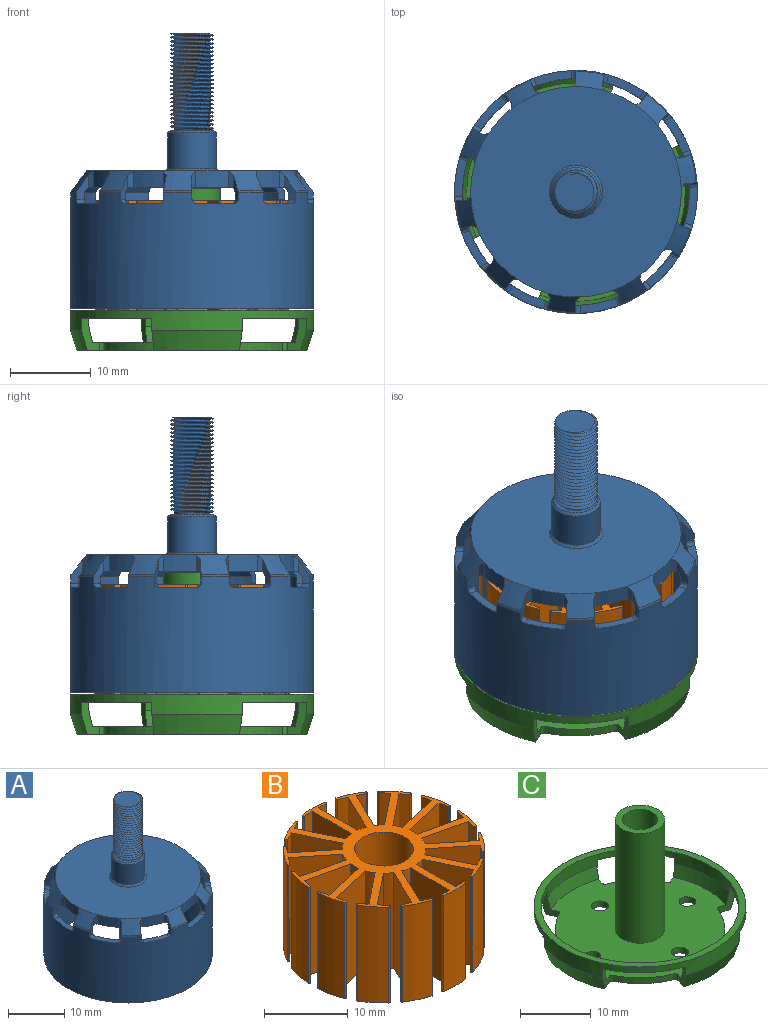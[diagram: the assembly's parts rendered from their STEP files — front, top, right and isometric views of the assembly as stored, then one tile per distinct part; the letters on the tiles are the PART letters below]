
ASSEMBLY  parts=3 mates=2
PART A: 126 faces, bbox 30.5x30.6x39.7 mm
  f0: bspline ~12.08x6.06mm, area 172.5mm2, adj f1,f2,f59,f60
  f1: bspline ~12.25x6.06mm, area 176.6mm2, adj f0,f2,f59,f60
  f2: cylinder r=2.2mm len=12mm, axis (0,0,-1), area -13.2mm2, adj f0,f1,f58,f59,f60
  f3: cylinder r=13mm len=4.02mm, axis (0,0,1), area 8.2mm2, adj f23,f56,f74,f75
  f4: cylinder r=13mm len=3mm, axis (0,0,1), area 8.2mm2, adj f23,f56,f71,f76
  f5: cylinder r=13mm len=4.07mm, axis (0,0,1), area 8.2mm2, adj f23,f56,f77,f78
  f6: cylinder r=13mm len=3.57mm, axis (0,0,1), area 8.2mm2, adj f23,f56,f79,f80
  f7: cylinder r=13mm len=3.72mm, axis (0,0,1), area 8.2mm2, adj f23,f56,f81,f82
  f8: cylinder r=13mm len=4.02mm, axis (0,0,1), area 8.2mm2, adj f23,f56,f83,f84
  f9: cylinder r=13mm len=3mm, axis (0,0,1), area 8.2mm2, adj f23,f56,f85,f86
  f10: cylinder r=13mm len=4.07mm, axis (0,0,1), area 8.2mm2, adj f23,f56,f87,f88
  f11: cylinder r=13mm len=3.57mm, axis (0,0,1), area 8.2mm2, adj f23,f56,f89,f90
  f12: cylinder r=13mm len=3.72mm, axis (0,0,1), area 8.2mm2, adj f23,f56,f72,f73
  f13: cone r=13mm half-angle=38.7deg, axis (0,0,-1), area 10.4mm2, adj f23,f26,f54,f73,f75,f120
  f14: cone r=13mm half-angle=38.7deg, axis (0,0,-1), area 10.4mm2, adj f23,f51,f53,f72,f89,f91
  f15: cone r=13mm half-angle=38.7deg, axis (0,0,-1), area 10.4mm2, adj f23,f48,f50,f88,f90,f94
  f16: cone r=13mm half-angle=38.7deg, axis (0,0,-1), area 10.4mm2, adj f23,f45,f47,f85,f87,f97
  f17: cone r=13mm half-angle=38.7deg, axis (0,0,-1), area 10.4mm2, adj f23,f42,f44,f83,f86,f100
  f18: cone r=13mm half-angle=38.7deg, axis (0,0,-1), area 10.4mm2, adj f23,f39,f41,f82,f84,f103
  f19: cone r=13mm half-angle=38.7deg, axis (0,0,-1), area 10.4mm2, adj f23,f36,f38,f79,f81,f106
  f20: cone r=13mm half-angle=38.7deg, axis (0,0,-1), area 10.4mm2, adj f23,f33,f35,f77,f80,f109
  f21: cone r=13mm half-angle=38.7deg, axis (0,0,-1), area 10.4mm2, adj f23,f30,f32,f71,f78,f112
  f22: cylinder r=15mm len=30mm, axis (0,0,-1), area 1275mm2, adj f25,f26,f27,f28,f29,f30,f31,f32
  f23: plane 26x26mm, normal (0,0,1), area 496.7mm2, adj f3,f4,f5,f6,f7,f8,f9,f10
  f24: cone r=13mm half-angle=38.7deg, axis (0,0,-1), area 10.4mm2, adj f23,f27,f29,f74,f76,f115
  f25: plane 4.74x1.86mm, normal (0,0,1), area 4.7mm2, adj f22,f55,f118,f119
  f26: plane 2.89x1.51mm, normal (1,0,0), area 2.3mm2, adj f13,f22,f55,f56,f70,f75,f119,f120
  f27: plane 2.89x1.4mm, normal (-0.92,-0.38,0), area 2.3mm2, adj f22,f24,f55,f56,f68,f74,f115,f118
  f28: plane 4.07x3.87mm, normal (0,0,1), area 4.7mm2, adj f22,f55,f116,f117
  f29: plane 2.89x1.22mm, normal (0.81,0.59,0), area 2.3mm2, adj f22,f24,f55,f56,f68,f76,f115,f117
  f30: plane 2.89x1.29mm, normal (-0.52,-0.85,0), area 2.3mm2, adj f21,f22,f55,f56,f67,f71,f112,f116
  f31: plane 4.8x1.54mm, normal (0,0,1), area 4.7mm2, adj f22,f55,f113,f114
  f32: plane 2.89x1.44mm, normal (0.31,0.95,0), area 2.3mm2, adj f21,f22,f55,f56,f67,f78,f112,f114
  f33: plane 2.89x1.51mm, normal (0.08,-1,0), area 2.3mm2, adj f20,f22,f55,f56,f61,f77,f109,f113
  f34: plane 4.53x3.12mm, normal (0,0,1), area 4.7mm2, adj f22,f55,f110,f111
  f35: plane 2.89x1.44mm, normal (-0.31,0.95,0), area 2.3mm2, adj f20,f22,f55,f56,f61,f80,f109,f111
  f36: plane 2.89x1.15mm, normal (0.65,-0.76,0), area 2.3mm2, adj f19,f22,f55,f56,f62,f79,f106,f110
  f37: plane 4.62x2.84mm, normal (0,0,1), area 4.7mm2, adj f22,f55,f107,f108
  f38: plane 2.89x1.22mm, normal (-0.81,0.59,0), area 2.3mm2, adj f19,f22,f55,f56,f62,f81,f106,f108
  f39: plane 2.89x1.47mm, normal (0.97,-0.24,0), area 2.3mm2, adj f18,f22,f55,f56,f63,f82,f103,f107
  f40: plane 4.74x1.86mm, normal (0,0,1), area 4.7mm2, adj f22,f55,f104,f105
  f41: plane 2.89x1.51mm, normal (-1,0,0), area 2.3mm2, adj f18,f22,f55,f56,f63,f84,f103,f105
  f42: plane 2.89x1.4mm, normal (0.92,0.38,0), area 2.3mm2, adj f17,f22,f55,f56,f64,f83,f100,f104
  f43: plane 4.07x3.87mm, normal (0,0,1), area 4.7mm2, adj f22,f55,f101,f102
  f44: plane 2.89x1.22mm, normal (-0.81,-0.59,0), area 2.3mm2, adj f17,f22,f55,f56,f64,f86,f100,f102
  f45: plane 2.89x1.29mm, normal (0.52,0.85,0), area 2.3mm2, adj f16,f22,f55,f56,f65,f85,f97,f101
  f46: plane 4.8x1.54mm, normal (0,0,1), area 4.7mm2, adj f22,f55,f98,f99
  f47: plane 2.89x1.44mm, normal (-0.31,-0.95,0), area 2.3mm2, adj f16,f22,f55,f56,f65,f87,f97,f99
  f48: plane 2.89x1.51mm, normal (-0.08,1,0), area 2.3mm2, adj f15,f22,f55,f56,f66,f88,f94,f98
  f49: plane 4.53x3.12mm, normal (0,0,1), area 4.7mm2, adj f22,f55,f95,f96
  f50: plane 2.89x1.44mm, normal (0.31,-0.95,0), area 2.3mm2, adj f15,f22,f55,f56,f66,f90,f94,f96
  f51: plane 2.89x1.15mm, normal (-0.65,0.76,0), area 2.3mm2, adj f14,f22,f55,f56,f69,f89,f91,f95
  f52: plane 4.62x2.84mm, normal (0,0,1), area 4.7mm2, adj f22,f55,f92,f93
  f53: plane 2.89x1.22mm, normal (0.81,-0.59,0), area 2.3mm2, adj f14,f22,f55,f56,f69,f72,f91,f93
  f54: plane 2.89x1.47mm, normal (-0.97,0.24,0), area 2.3mm2, adj f13,f22,f55,f56,f70,f73,f92,f120
  f55: cylinder r=14mm len=28mm, axis (0,0,-1), area 1189.4mm2, adj f25,f26,f27,f28,f29,f30,f31,f32
  f56: plane 27x26.92mm, normal (0,0,-1), area 542mm2, adj f3,f4,f5,f6,f7,f8,f9,f10
  f57: cylinder r=3mm len=6mm, axis (0,0,-1), area 82.9mm2, adj f121,f122
  f58: plane 5.4x5.4mm, normal (0,0,1), area 7.7mm2, adj f2,f122
  f59: plane 5.17x5.17mm, normal (0,0,1), area 18.3mm2, adj f0,f1,f2
  f60: plane 0.49x0.42mm, normal (0,1,0), area 0.1mm2, adj f0,f1,f2
  f61: cone r=13.5mm half-angle=35.5deg, axis (0,0,-1), area 2.8mm2, adj f33,f35,f55,f56
  f62: cone r=13.5mm half-angle=35.5deg, axis (0,0,-1), area 2.8mm2, adj f36,f38,f55,f56
  f63: cone r=13.5mm half-angle=35.5deg, axis (0,0,-1), area 2.8mm2, adj f39,f41,f55,f56
  f64: cone r=13.5mm half-angle=35.5deg, axis (0,0,-1), area 2.8mm2, adj f42,f44,f55,f56
  f65: cone r=13.5mm half-angle=35.5deg, axis (0,0,-1), area 2.8mm2, adj f45,f47,f55,f56
  f66: cone r=13.5mm half-angle=35.5deg, axis (0,0,-1), area 2.8mm2, adj f48,f50,f55,f56
  f67: cone r=13.5mm half-angle=35.5deg, axis (0,0,-1), area 2.8mm2, adj f30,f32,f55,f56
  f68: cone r=13.5mm half-angle=35.5deg, axis (0,0,-1), area 2.8mm2, adj f27,f29,f55,f56
  f69: cone r=13.5mm half-angle=35.5deg, axis (0,0,-1), area 2.8mm2, adj f51,f53,f55,f56
  f70: cone r=13.5mm half-angle=35.5deg, axis (0,0,-1), area 2.8mm2, adj f26,f54,f55,f56
  f71: plane 2.01x0.69mm, normal (0.21,-0.98,0), area 1.2mm2, adj f4,f21,f30,f56
  f72: plane 2.01x0.7mm, normal (0.17,-0.98,0), area 1.2mm2, adj f12,f14,f53,f56
  f73: plane 2.01x0.61mm, normal (-0.86,-0.5,0), area 1.2mm2, adj f12,f13,f54,f56
  f74: plane 2.01x0.65mm, normal (-0.4,-0.92,0), area 1.2mm2, adj f3,f24,f27,f56
  f75: plane 2.01x0.51mm, normal (0.72,-0.69,0), area 1.2mm2, adj f3,f13,f26,f56
  f76: plane 2.01x0.7mm, normal (0.99,-0.14,0), area 1.2mm2, adj f4,f24,f29,f56
  f77: plane 2.01x0.53mm, normal (0.75,-0.67,0), area 1.2mm2, adj f5,f20,f33,f56
  f78: plane 2.01x0.62mm, normal (0.88,0.47,0), area 1.2mm2, adj f5,f21,f32,f56
  f79: plane 2.01x0.7mm, normal (1,-0.1,0), area 1.2mm2, adj f6,f19,f36,f56
  f80: plane 2.01x0.64mm, normal (0.44,0.9,0), area 1.2mm2, adj f6,f20,f35,f56
  f81: plane 2.01x0.7mm, normal (-0.17,0.98,0), area 1.2mm2, adj f7,f19,f38,f56
  f82: plane 2.01x0.61mm, normal (0.86,0.5,0), area 1.2mm2, adj f7,f18,f39,f56
  f83: plane 2.01x0.65mm, normal (0.4,0.92,0), area 1.2mm2, adj f8,f17,f42,f56
  f84: plane 2.01x0.51mm, normal (-0.72,0.69,0), area 1.2mm2, adj f8,f18,f41,f56
  f85: plane 2.01x0.69mm, normal (-0.21,0.98,0), area 1.2mm2, adj f9,f16,f45,f56
  f86: plane 2.01x0.7mm, normal (-0.99,0.14,0), area 1.2mm2, adj f9,f17,f44,f56
  f87: plane 2.01x0.62mm, normal (-0.88,-0.47,0), area 1.2mm2, adj f10,f16,f47,f56
  f88: plane 2.01x0.53mm, normal (-0.75,0.67,0), area 1.2mm2, adj f10,f15,f48,f56
  f89: plane 2.01x0.7mm, normal (-1,0.1,0), area 1.2mm2, adj f11,f14,f51,f56
  f90: plane 2.01x0.64mm, normal (-0.44,-0.9,0), area 1.2mm2, adj f11,f15,f50,f56
  f91: torus R=14.5mm, axis (0,0,1), area 1.2mm2, adj f14,f22,f51,f53
  f92: cylinder r=0.5mm len=1.1mm, axis (0.24,0.97,0), area 0.8mm2, adj f22,f52,f54,f55
  f93: cylinder r=0.5mm len=1.11mm, axis (-0.59,-0.81,0), area 0.8mm2, adj f22,f52,f53,f55
  f94: torus R=14.5mm, axis (0,0,1), area 1.2mm2, adj f15,f22,f48,f50
  f95: cylinder r=0.5mm len=1.09mm, axis (0.76,0.65,0), area 0.8mm2, adj f22,f49,f51,f55
  f96: cylinder r=0.5mm len=1.11mm, axis (-0.95,-0.31,0), area 0.8mm2, adj f22,f49,f50,f55
  f97: torus R=14.5mm, axis (0,0,1), area 1.2mm2, adj f16,f22,f45,f47
  f98: cylinder r=0.5mm len=1.04mm, axis (1,0.08,0), area 0.8mm2, adj f22,f46,f48,f55
  f99: cylinder r=0.5mm len=1.11mm, axis (-0.95,0.31,0), area 0.8mm2, adj f22,f46,f47,f55
  f100: torus R=14.5mm, axis (0,0,1), area 1.2mm2, adj f17,f22,f42,f44
  f101: cylinder r=0.5mm len=1.12mm, axis (0.85,-0.52,0), area 0.8mm2, adj f22,f43,f45,f55
  f102: cylinder r=0.5mm len=1.11mm, axis (-0.59,0.81,0), area 0.8mm2, adj f22,f43,f44,f55
  f103: torus R=14.5mm, axis (0,0,1), area 1.2mm2, adj f18,f22,f39,f41
  f104: cylinder r=0.5mm len=1.12mm, axis (0.38,-0.92,0), area 0.8mm2, adj f22,f40,f42,f55
  f105: cylinder r=0.5mm len=1.01mm, axis (0,1,0), area 0.8mm2, adj f22,f40,f41,f55
  f106: torus R=14.5mm, axis (0,0,1), area 1.2mm2, adj f19,f22,f36,f38
  f107: cylinder r=0.5mm len=1.1mm, axis (-0.24,-0.97,0), area 0.8mm2, adj f22,f37,f39,f55
  f108: cylinder r=0.5mm len=1.11mm, axis (0.59,0.81,0), area 0.8mm2, adj f22,f37,f38,f55
  f109: torus R=14.5mm, axis (0,0,1), area 1.2mm2, adj f20,f22,f33,f35
  f110: cylinder r=0.5mm len=1.09mm, axis (-0.76,-0.65,0), area 0.8mm2, adj f22,f34,f36,f55
  f111: cylinder r=0.5mm len=1.11mm, axis (0.95,0.31,0), area 0.8mm2, adj f22,f34,f35,f55
  f112: torus R=14.5mm, axis (0,0,1), area 1.2mm2, adj f21,f22,f30,f32
  f113: cylinder r=0.5mm len=1.04mm, axis (-1,-0.08,0), area 0.8mm2, adj f22,f31,f33,f55
  f114: cylinder r=0.5mm len=1.11mm, axis (0.95,-0.31,0), area 0.8mm2, adj f22,f31,f32,f55
  f115: torus R=14.5mm, axis (0,0,1), area 1.2mm2, adj f22,f24,f27,f29
  f116: cylinder r=0.5mm len=1.12mm, axis (-0.85,0.52,0), area 0.8mm2, adj f22,f28,f30,f55
  f117: cylinder r=0.5mm len=1.11mm, axis (0.59,-0.81,0), area 0.8mm2, adj f22,f28,f29,f55
  f118: cylinder r=0.5mm len=1.12mm, axis (-0.38,0.92,0), area 0.8mm2, adj f22,f25,f27,f55
  f119: cylinder r=0.5mm len=1.01mm, axis (0,-1,0), area 0.8mm2, adj f22,f25,f26,f55
  f120: torus R=14.5mm, axis (0,0,1), area 1.2mm2, adj f13,f22,f26,f54
  f121: cone r=3mm half-angle=45deg, axis (0,0,-1), area 8.4mm2, adj f23,f57
  f122: cone r=2.7mm half-angle=45deg, axis (0,0,-1), area 7.6mm2, adj f57,f58
  f123: cylinder r=1.5mm len=20mm, axis (0,0,1), area 188.5mm2, adj f56,f124
  f124: plane 3x3mm, normal (0,0,-1), area 7.1mm2, adj f123
  f125: plane 30x30mm, normal (0,0,-1), area 91.1mm2, adj f22,f55
PART B: 171 faces, bbox 24x24x14 mm
  f0: cylinder r=5mm len=14mm, axis (0,0,-1), area 17.4mm2, adj f15,f154,f164,f170
  f1: cylinder r=5mm len=14mm, axis (0,0,-1), area 17.4mm2, adj f15,f143,f153,f170
  f2: cylinder r=5mm len=14mm, axis (0,0,-1), area 17.4mm2, adj f15,f132,f142,f170
  f3: cylinder r=5mm len=14mm, axis (0,0,-1), area 17.4mm2, adj f15,f121,f131,f170
  f4: cylinder r=5mm len=14mm, axis (0,0,-1), area 17.4mm2, adj f15,f110,f120,f170
  f5: cylinder r=5mm len=14mm, axis (0,0,-1), area 17.4mm2, adj f15,f99,f109,f170
  f6: cylinder r=5mm len=14mm, axis (0,0,-1), area 17.4mm2, adj f15,f88,f98,f170
  f7: cylinder r=5mm len=14mm, axis (0,0,-1), area 17.4mm2, adj f15,f77,f87,f170
  f8: cylinder r=5mm len=14mm, axis (0,0,-1), area 17.4mm2, adj f15,f66,f76,f170
  f9: cylinder r=5mm len=14mm, axis (0,0,-1), area 17.4mm2, adj f15,f55,f65,f170
  f10: cylinder r=5mm len=14mm, axis (0,0,-1), area 17.4mm2, adj f15,f44,f54,f170
  f11: cylinder r=5mm len=14mm, axis (0,0,-1), area 17.4mm2, adj f15,f33,f43,f170
  f12: cylinder r=5mm len=14mm, axis (0,0,-1), area 17.4mm2, adj f15,f22,f32,f170
  f13: cylinder r=5mm len=14mm, axis (0,0,-1), area 17.4mm2, adj f15,f21,f165,f170
  f14: cylinder r=3.5mm len=14mm, axis (0,0,-1), area 307.9mm2, adj f15,f170
  f15: plane 24x23.95mm, normal (0,0,-1), area 154.9mm2, adj f0,f1,f2,f3,f4,f5,f6,f7
  f16: plane 14x1.4mm, normal (0,-1,0), area 19.5mm2, adj f15,f22,f23,f170
  f17: plane 14x0.04mm, normal (-1,0,0), area 0.5mm2, adj f15,f23,f24,f170
  f18: cylinder r=12mm len=14mm, axis (0,0,-1), area 52.5mm2, adj f15,f24,f26,f170
  f19: plane 14x0.03mm, normal (1,0,0), area 0.5mm2, adj f15,f25,f26,f170
  f20: plane 14x1.29mm, normal (0,-1,0), area 18.1mm2, adj f15,f21,f25,f170
  f21: plane 14x6.55mm, normal (1,0,0), area 91.8mm2, adj f13,f15,f20,f170
  f22: plane 14x6.54mm, normal (-1,0,0), area 91.5mm2, adj f12,f15,f16,f170
  f23: cylinder r=0.15mm len=14mm, axis (0,0,-1), area 3.3mm2, adj f15,f16,f17,f170
  f24: cylinder r=0.15mm len=14mm, axis (0,0,-1), area 3mm2, adj f15,f17,f18,f170
  f25: cylinder r=0.15mm len=14mm, axis (0,0,-1), area 3.3mm2, adj f15,f19,f20,f170
  f26: cylinder r=0.15mm len=14mm, axis (0,0,-1), area 3mm2, adj f15,f18,f19,f170
  f27: plane 14x1.26mm, normal (0.43,-0.9,0), area 19.5mm2, adj f15,f33,f34,f170
  f28: plane 14x0.03mm, normal (-0.9,-0.43,0), area 0.5mm2, adj f15,f34,f35,f170
  f29: cylinder r=12mm len=14mm, axis (0,0,-1), area 52.5mm2, adj f15,f35,f37,f170
  f30: plane 14x0.03mm, normal (0.9,0.43,0), area 0.5mm2, adj f15,f36,f37,f170
  f31: plane 14x1.17mm, normal (0.43,-0.9,0), area 18.1mm2, adj f15,f32,f36,f170
  f32: plane 14x5.9mm, normal (0.9,0.43,0), area 91.8mm2, adj f12,f15,f31,f170
  f33: plane 14x5.89mm, normal (-0.9,-0.43,0), area 91.5mm2, adj f11,f15,f27,f170
  f34: cylinder r=0.15mm len=14mm, axis (0,0,-1), area 3.3mm2, adj f15,f27,f28,f170
  f35: cylinder r=0.15mm len=14mm, axis (0,0,-1), area 3mm2, adj f15,f28,f29,f170
  f36: cylinder r=0.15mm len=14mm, axis (0,0,-1), area 3.3mm2, adj f15,f30,f31,f170
  f37: cylinder r=0.15mm len=14mm, axis (0,0,-1), area 3mm2, adj f15,f29,f30,f170
  f38: plane 14x1.09mm, normal (0.78,-0.62,0), area 19.5mm2, adj f15,f44,f45,f170
  f39: plane 14x0.03mm, normal (-0.62,-0.78,0), area 0.5mm2, adj f15,f45,f46,f170
  f40: cylinder r=12mm len=14mm, axis (0,0,-1), area 52.5mm2, adj f15,f46,f48,f170
  f41: plane 14x0.03mm, normal (0.62,0.78,0), area 0.5mm2, adj f15,f47,f48,f170
  f42: plane 14x1.01mm, normal (0.78,-0.62,0), area 18.1mm2, adj f15,f43,f47,f170
  f43: plane 14x5.12mm, normal (0.62,0.78,0), area 91.8mm2, adj f11,f15,f42,f170
  f44: plane 14x5.11mm, normal (-0.62,-0.78,0), area 91.5mm2, adj f10,f15,f38,f170
  f45: cylinder r=0.15mm len=14mm, axis (0,0,-1), area 3.3mm2, adj f15,f38,f39,f170
  f46: cylinder r=0.15mm len=14mm, axis (0,0,-1), area 3mm2, adj f15,f39,f40,f170
  f47: cylinder r=0.15mm len=14mm, axis (0,0,-1), area 3.3mm2, adj f15,f41,f42,f170
  f48: cylinder r=0.15mm len=14mm, axis (0,0,-1), area 3mm2, adj f15,f40,f41,f170
  f49: plane 14x1.36mm, normal (0.97,-0.22,0), area 19.5mm2, adj f15,f55,f56,f170
  f50: plane 14x0.04mm, normal (-0.22,-0.97,0), area 0.5mm2, adj f15,f56,f57,f170
  f51: cylinder r=12mm len=14mm, axis (0,0,-1), area 52.5mm2, adj f15,f57,f59,f170
  f52: plane 14x0.03mm, normal (0.22,0.97,0), area 0.5mm2, adj f15,f58,f59,f170
  f53: plane 14x1.26mm, normal (0.97,-0.22,0), area 18.1mm2, adj f15,f54,f58,f170
  f54: plane 14x6.39mm, normal (0.22,0.97,0), area 91.8mm2, adj f10,f15,f53,f170
  f55: plane 14x6.37mm, normal (-0.22,-0.97,0), area 91.5mm2, adj f9,f15,f49,f170
  f56: cylinder r=0.15mm len=14mm, axis (0,0,-1), area 3.3mm2, adj f15,f49,f50,f170
  f57: cylinder r=0.15mm len=14mm, axis (0,0,-1), area 3mm2, adj f15,f50,f51,f170
  f58: cylinder r=0.15mm len=14mm, axis (0,0,-1), area 3.3mm2, adj f15,f52,f53,f170
  f59: cylinder r=0.15mm len=14mm, axis (0,0,-1), area 3mm2, adj f15,f51,f52,f170
  f60: plane 14x1.36mm, normal (0.97,0.22,0), area 19.5mm2, adj f15,f66,f67,f170
  f61: plane 14x0.04mm, normal (0.22,-0.97,0), area 0.5mm2, adj f15,f67,f68,f170
  f62: cylinder r=12mm len=14mm, axis (0,0,-1), area 52.5mm2, adj f15,f68,f70,f170
  f63: plane 14x0.03mm, normal (-0.22,0.97,0), area 0.5mm2, adj f15,f69,f70,f170
  f64: plane 14x1.26mm, normal (0.97,0.22,0), area 18.1mm2, adj f15,f65,f69,f170
  f65: plane 14x6.39mm, normal (-0.22,0.97,0), area 91.8mm2, adj f9,f15,f64,f170
  f66: plane 14x6.37mm, normal (0.22,-0.97,0), area 91.5mm2, adj f8,f15,f60,f170
  f67: cylinder r=0.15mm len=14mm, axis (0,0,-1), area 3.3mm2, adj f15,f60,f61,f170
  f68: cylinder r=0.15mm len=14mm, axis (0,0,-1), area 3mm2, adj f15,f61,f62,f170
  f69: cylinder r=0.15mm len=14mm, axis (0,0,-1), area 3.3mm2, adj f15,f63,f64,f170
  f70: cylinder r=0.15mm len=14mm, axis (0,0,-1), area 3mm2, adj f15,f62,f63,f170
  f71: plane 14x1.09mm, normal (0.78,0.62,0), area 19.5mm2, adj f15,f77,f78,f170
  f72: plane 14x0.03mm, normal (0.62,-0.78,0), area 0.5mm2, adj f15,f78,f79,f170
  f73: cylinder r=12mm len=14mm, axis (0,0,-1), area 52.5mm2, adj f15,f79,f81,f170
  f74: plane 14x0.03mm, normal (-0.62,0.78,0), area 0.5mm2, adj f15,f80,f81,f170
  f75: plane 14x1.01mm, normal (0.78,0.62,0), area 18.1mm2, adj f15,f76,f80,f170
  f76: plane 14x5.12mm, normal (-0.62,0.78,0), area 91.8mm2, adj f8,f15,f75,f170
  f77: plane 14x5.11mm, normal (0.62,-0.78,0), area 91.5mm2, adj f7,f15,f71,f170
  f78: cylinder r=0.15mm len=14mm, axis (0,0,-1), area 3.3mm2, adj f15,f71,f72,f170
  f79: cylinder r=0.15mm len=14mm, axis (0,0,-1), area 3mm2, adj f15,f72,f73,f170
  f80: cylinder r=0.15mm len=14mm, axis (0,0,-1), area 3.3mm2, adj f15,f74,f75,f170
  f81: cylinder r=0.15mm len=14mm, axis (0,0,-1), area 3mm2, adj f15,f73,f74,f170
  f82: plane 14x1.26mm, normal (0.43,0.9,0), area 19.5mm2, adj f15,f88,f89,f170
  f83: plane 14x0.03mm, normal (0.9,-0.43,0), area 0.5mm2, adj f15,f89,f90,f170
  f84: cylinder r=12mm len=14mm, axis (0,0,-1), area 52.5mm2, adj f15,f90,f92,f170
  f85: plane 14x0.03mm, normal (-0.9,0.43,0), area 0.5mm2, adj f15,f91,f92,f170
  f86: plane 14x1.17mm, normal (0.43,0.9,0), area 18.1mm2, adj f15,f87,f91,f170
  f87: plane 14x5.9mm, normal (-0.9,0.43,0), area 91.8mm2, adj f7,f15,f86,f170
  f88: plane 14x5.89mm, normal (0.9,-0.43,0), area 91.5mm2, adj f6,f15,f82,f170
  f89: cylinder r=0.15mm len=14mm, axis (0,0,-1), area 3.3mm2, adj f15,f82,f83,f170
  f90: cylinder r=0.15mm len=14mm, axis (0,0,-1), area 3mm2, adj f15,f83,f84,f170
  f91: cylinder r=0.15mm len=14mm, axis (0,0,-1), area 3.3mm2, adj f15,f85,f86,f170
  f92: cylinder r=0.15mm len=14mm, axis (0,0,-1), area 3mm2, adj f15,f84,f85,f170
  f93: plane 14x1.4mm, normal (0,1,0), area 19.5mm2, adj f15,f99,f100,f170
  f94: plane 14x0.04mm, normal (1,0,0), area 0.5mm2, adj f15,f100,f101,f170
  f95: cylinder r=12mm len=14mm, axis (0,0,-1), area 52.5mm2, adj f15,f101,f103,f170
  f96: plane 14x0.03mm, normal (-1,0,0), area 0.5mm2, adj f15,f102,f103,f170
  f97: plane 14x1.29mm, normal (0,1,0), area 18.1mm2, adj f15,f98,f102,f170
  f98: plane 14x6.55mm, normal (-1,0,0), area 91.8mm2, adj f6,f15,f97,f170
  f99: plane 14x6.54mm, normal (1,0,0), area 91.5mm2, adj f5,f15,f93,f170
  f100: cylinder r=0.15mm len=14mm, axis (0,0,-1), area 3.3mm2, adj f15,f93,f94,f170
  f101: cylinder r=0.15mm len=14mm, axis (0,0,-1), area 3mm2, adj f15,f94,f95,f170
  f102: cylinder r=0.15mm len=14mm, axis (0,0,-1), area 3.3mm2, adj f15,f96,f97,f170
  f103: cylinder r=0.15mm len=14mm, axis (0,0,-1), area 3mm2, adj f15,f95,f96,f170
  f104: plane 14x1.26mm, normal (-0.43,0.9,0), area 19.5mm2, adj f15,f110,f111,f170
  f105: plane 14x0.03mm, normal (0.9,0.43,0), area 0.5mm2, adj f15,f111,f112,f170
  f106: cylinder r=12mm len=14mm, axis (0,0,-1), area 52.5mm2, adj f15,f112,f114,f170
  f107: plane 14x0.03mm, normal (-0.9,-0.43,0), area 0.5mm2, adj f15,f113,f114,f170
  f108: plane 14x1.17mm, normal (-0.43,0.9,0), area 18.1mm2, adj f15,f109,f113,f170
  f109: plane 14x5.9mm, normal (-0.9,-0.43,0), area 91.8mm2, adj f5,f15,f108,f170
  f110: plane 14x5.89mm, normal (0.9,0.43,0), area 91.5mm2, adj f4,f15,f104,f170
  f111: cylinder r=0.15mm len=14mm, axis (0,0,-1), area 3.3mm2, adj f15,f104,f105,f170
  f112: cylinder r=0.15mm len=14mm, axis (0,0,-1), area 3mm2, adj f15,f105,f106,f170
  f113: cylinder r=0.15mm len=14mm, axis (0,0,-1), area 3.3mm2, adj f15,f107,f108,f170
  f114: cylinder r=0.15mm len=14mm, axis (0,0,-1), area 3mm2, adj f15,f106,f107,f170
  f115: plane 14x1.09mm, normal (-0.78,0.62,0), area 19.5mm2, adj f15,f121,f122,f170
  f116: plane 14x0.03mm, normal (0.62,0.78,0), area 0.5mm2, adj f15,f122,f123,f170
  f117: cylinder r=12mm len=14mm, axis (0,0,-1), area 52.5mm2, adj f15,f123,f125,f170
  f118: plane 14x0.03mm, normal (-0.62,-0.78,0), area 0.5mm2, adj f15,f124,f125,f170
  f119: plane 14x1.01mm, normal (-0.78,0.62,0), area 18.1mm2, adj f15,f120,f124,f170
  f120: plane 14x5.12mm, normal (-0.62,-0.78,0), area 91.8mm2, adj f4,f15,f119,f170
  f121: plane 14x5.11mm, normal (0.62,0.78,0), area 91.5mm2, adj f3,f15,f115,f170
  f122: cylinder r=0.15mm len=14mm, axis (0,0,-1), area 3.3mm2, adj f15,f115,f116,f170
  f123: cylinder r=0.15mm len=14mm, axis (0,0,-1), area 3mm2, adj f15,f116,f117,f170
  f124: cylinder r=0.15mm len=14mm, axis (0,0,-1), area 3.3mm2, adj f15,f118,f119,f170
  f125: cylinder r=0.15mm len=14mm, axis (0,0,-1), area 3mm2, adj f15,f117,f118,f170
  f126: plane 14x1.36mm, normal (-0.97,0.22,0), area 19.5mm2, adj f15,f132,f133,f170
  f127: plane 14x0.04mm, normal (0.22,0.97,0), area 0.5mm2, adj f15,f133,f134,f170
  f128: cylinder r=12mm len=14mm, axis (0,0,-1), area 52.5mm2, adj f15,f134,f136,f170
  f129: plane 14x0.03mm, normal (-0.22,-0.97,0), area 0.5mm2, adj f15,f135,f136,f170
  f130: plane 14x1.26mm, normal (-0.97,0.22,0), area 18.1mm2, adj f15,f131,f135,f170
  f131: plane 14x6.39mm, normal (-0.22,-0.97,0), area 91.8mm2, adj f3,f15,f130,f170
  f132: plane 14x6.37mm, normal (0.22,0.97,0), area 91.5mm2, adj f2,f15,f126,f170
  f133: cylinder r=0.15mm len=14mm, axis (0,0,-1), area 3.3mm2, adj f15,f126,f127,f170
  f134: cylinder r=0.15mm len=14mm, axis (0,0,-1), area 3mm2, adj f15,f127,f128,f170
  f135: cylinder r=0.15mm len=14mm, axis (0,0,-1), area 3.3mm2, adj f15,f129,f130,f170
  f136: cylinder r=0.15mm len=14mm, axis (0,0,-1), area 3mm2, adj f15,f128,f129,f170
  f137: plane 14x1.36mm, normal (-0.97,-0.22,0), area 19.5mm2, adj f15,f143,f144,f170
  f138: plane 14x0.04mm, normal (-0.22,0.97,0), area 0.5mm2, adj f15,f144,f145,f170
  f139: cylinder r=12mm len=14mm, axis (0,0,-1), area 52.5mm2, adj f15,f145,f147,f170
  f140: plane 14x0.03mm, normal (0.22,-0.97,0), area 0.5mm2, adj f15,f146,f147,f170
  f141: plane 14x1.26mm, normal (-0.97,-0.22,0), area 18.1mm2, adj f15,f142,f146,f170
  f142: plane 14x6.39mm, normal (0.22,-0.97,0), area 91.8mm2, adj f2,f15,f141,f170
  f143: plane 14x6.37mm, normal (-0.22,0.97,0), area 91.5mm2, adj f1,f15,f137,f170
  f144: cylinder r=0.15mm len=14mm, axis (0,0,-1), area 3.3mm2, adj f15,f137,f138,f170
  f145: cylinder r=0.15mm len=14mm, axis (0,0,-1), area 3mm2, adj f15,f138,f139,f170
  f146: cylinder r=0.15mm len=14mm, axis (0,0,-1), area 3.3mm2, adj f15,f140,f141,f170
  f147: cylinder r=0.15mm len=14mm, axis (0,0,-1), area 3mm2, adj f15,f139,f140,f170
  f148: plane 14x1.09mm, normal (-0.78,-0.62,0), area 19.5mm2, adj f15,f154,f155,f170
  f149: plane 14x0.03mm, normal (-0.62,0.78,0), area 0.5mm2, adj f15,f155,f156,f170
  f150: cylinder r=12mm len=14mm, axis (0,0,-1), area 52.5mm2, adj f15,f156,f158,f170
  f151: plane 14x0.03mm, normal (0.62,-0.78,0), area 0.5mm2, adj f15,f157,f158,f170
  f152: plane 14x1.01mm, normal (-0.78,-0.62,0), area 18.1mm2, adj f15,f153,f157,f170
  f153: plane 14x5.12mm, normal (0.62,-0.78,0), area 91.8mm2, adj f1,f15,f152,f170
  f154: plane 14x5.11mm, normal (-0.62,0.78,0), area 91.5mm2, adj f0,f15,f148,f170
  f155: cylinder r=0.15mm len=14mm, axis (0,0,-1), area 3.3mm2, adj f15,f148,f149,f170
  f156: cylinder r=0.15mm len=14mm, axis (0,0,-1), area 3mm2, adj f15,f149,f150,f170
  f157: cylinder r=0.15mm len=14mm, axis (0,0,-1), area 3.3mm2, adj f15,f151,f152,f170
  f158: cylinder r=0.15mm len=14mm, axis (0,0,-1), area 3mm2, adj f15,f150,f151,f170
  f159: plane 14x1.26mm, normal (-0.43,-0.9,0), area 19.5mm2, adj f15,f165,f166,f170
  f160: plane 14x0.03mm, normal (-0.9,0.43,0), area 0.5mm2, adj f15,f166,f167,f170
  f161: cylinder r=12mm len=14mm, axis (0,0,-1), area 52.5mm2, adj f15,f167,f169,f170
  f162: plane 14x0.03mm, normal (0.9,-0.43,0), area 0.5mm2, adj f15,f168,f169,f170
  f163: plane 14x1.17mm, normal (-0.43,-0.9,0), area 18.1mm2, adj f15,f164,f168,f170
  f164: plane 14x5.9mm, normal (0.9,-0.43,0), area 91.8mm2, adj f0,f15,f163,f170
  f165: plane 14x5.89mm, normal (-0.9,0.43,0), area 91.5mm2, adj f13,f15,f159,f170
  f166: cylinder r=0.15mm len=14mm, axis (0,0,-1), area 3.3mm2, adj f15,f159,f160,f170
  f167: cylinder r=0.15mm len=14mm, axis (0,0,-1), area 3mm2, adj f15,f160,f161,f170
  f168: cylinder r=0.15mm len=14mm, axis (0,0,-1), area 3.3mm2, adj f15,f162,f163,f170
  f169: cylinder r=0.15mm len=14mm, axis (0,0,-1), area 3mm2, adj f15,f161,f162,f170
  f170: plane 24x23.95mm, normal (0,0,1), area 154.9mm2, adj f0,f1,f2,f3,f4,f5,f6,f7
PART C: 46 faces, bbox 30x30x20 mm
  f0: cylinder r=15mm len=30mm, axis (0,0,-1), area 163mm2, adj f10,f11,f12,f13,f15,f16,f17,f19
  f1: cylinder r=0.5mm len=1mm, axis (0,0,-1), area 0.8mm2, adj f9,f28,f30,f40
  f2: cylinder r=0.5mm len=1mm, axis (0,0,-1), area 0.8mm2, adj f9,f29,f30,f40
  f3: cylinder r=0.5mm len=1mm, axis (0,0,-1), area 0.8mm2, adj f9,f24,f26,f40
  f4: cylinder r=0.5mm len=1mm, axis (0,0,-1), area 0.8mm2, adj f9,f25,f26,f40
  f5: cylinder r=0.5mm len=1mm, axis (0,0,-1), area 0.8mm2, adj f9,f20,f22,f40
  f6: cylinder r=0.5mm len=1mm, axis (0,0,-1), area 0.8mm2, adj f9,f21,f22,f40
  f7: cylinder r=0.5mm len=1mm, axis (0,0,-1), area 0.8mm2, adj f9,f16,f18,f40
  f8: cylinder r=0.5mm len=1mm, axis (0,0,-1), area 0.8mm2, adj f9,f17,f18,f40
  f9: plane 28.4x28.4mm, normal (0,0,-1), area 484.2mm2, adj f1,f2,f3,f4,f5,f6,f7,f8
  f10: cone r=15mm half-angle=17.7deg, axis (0,0,1), area 29.3mm2, adj f0,f9,f25,f28
  f11: cone r=15mm half-angle=17.7deg, axis (0,0,1), area 29.3mm2, adj f0,f9,f21,f24
  f12: cone r=15mm half-angle=17.7deg, axis (0,0,1), area 29.3mm2, adj f0,f9,f17,f20
  f13: cone r=15mm half-angle=17.7deg, axis (0,0,1), area 29.3mm2, adj f0,f9,f16,f29
  f14: cylinder r=14mm len=28mm, axis (0,0,1), area 130.7mm2, adj f15,f16,f17,f19,f20,f21,f23,f24
  f15: plane 9.03x8.36mm, normal (0,0,-1), area 11.7mm2, adj f0,f14,f16,f17
  f16: plane 4x2.37mm, normal (-0.94,0.33,0), area 5mm2, adj f0,f7,f9,f13,f14,f15,f40,f44
  f17: plane 4x2.29mm, normal (0.41,-0.91,0), area 5mm2, adj f0,f8,f9,f12,f14,f15,f40,f45
  f18: cylinder r=12mm len=6.3mm, axis (0,0,-1), area 8.7mm2, adj f7,f8,f9,f40
  f19: plane 9.03x8.36mm, normal (0,0,-1), area 11.7mm2, adj f0,f14,f20,f21
  f20: plane 4x2.37mm, normal (0.33,0.94,0), area 5mm2, adj f0,f5,f9,f12,f14,f19,f40,f45
  f21: plane 4x2.29mm, normal (-0.91,-0.41,0), area 5mm2, adj f0,f6,f9,f11,f14,f19,f40,f43
  f22: cylinder r=12mm len=6.3mm, axis (0,0,-1), area 8.7mm2, adj f5,f6,f9,f40
  f23: plane 9.03x8.36mm, normal (0,0,-1), area 11.7mm2, adj f0,f14,f24,f25
  f24: plane 4x2.37mm, normal (0.94,-0.33,0), area 5mm2, adj f0,f3,f9,f11,f14,f23,f40,f43
  f25: plane 4x2.29mm, normal (-0.41,0.91,0), area 5mm2, adj f0,f4,f9,f10,f14,f23,f40,f42
  f26: cylinder r=12mm len=6.3mm, axis (0,0,-1), area 8.7mm2, adj f3,f4,f9,f40
  f27: plane 9.03x8.36mm, normal (0,0,-1), area 11.7mm2, adj f0,f14,f28,f29
  f28: plane 4x2.37mm, normal (-0.33,-0.94,0), area 5mm2, adj f0,f1,f9,f10,f14,f27,f40,f42
  f29: plane 4x2.29mm, normal (0.91,0.41,0), area 5mm2, adj f0,f2,f9,f13,f14,f27,f40,f44
  f30: cylinder r=12mm len=6.3mm, axis (0,0,-1), area 8.7mm2, adj f1,f2,f9,f40
  f31: cylinder r=2.5mm len=19.5mm, axis (0,0,-1), area 306.3mm2, adj f33,f35
  f32: cylinder r=3.5mm len=19mm, axis (0,0,-1), area 417.8mm2, adj f33,f40
  f33: plane 7x7mm, normal (0,0,1), area 18.8mm2, adj f31,f32
  f34: cylinder r=3.5mm len=7mm, axis (0,0,-1), area 11mm2, adj f9,f35
  f35: plane 7x7mm, normal (0,0,-1), area 18.8mm2, adj f31,f34
  f36: cylinder r=1.2mm len=2.4mm, axis (0,0,-1), area 7.5mm2, adj f9,f40
  f37: cylinder r=1.2mm len=2.4mm, axis (0,0,-1), area 7.5mm2, adj f9,f40
  f38: cylinder r=1.2mm len=2.4mm, axis (0,0,-1), area 7.5mm2, adj f9,f40
  f39: cylinder r=1.2mm len=2.4mm, axis (0,0,-1), area 7.5mm2, adj f9,f40
  f40: plane 27x27mm, normal (0,0,1), area 454.6mm2, adj f1,f2,f3,f4,f5,f6,f7,f8
  f41: plane 30x30mm, normal (0,0,1), area 91.1mm2, adj f0,f14
  f42: cone r=13.5mm half-angle=14deg, axis (0,0,1), area 21.6mm2, adj f14,f25,f28,f40
  f43: cone r=13.5mm half-angle=14deg, axis (0,0,1), area 21.6mm2, adj f14,f21,f24,f40
  f44: cone r=13.5mm half-angle=14deg, axis (0,0,1), area 21.6mm2, adj f14,f16,f29,f40
  f45: cone r=13.5mm half-angle=14deg, axis (0,0,1), area 21.6mm2, adj f14,f17,f20,f40
PLACE A rot(axis=(1,0,0),0deg) t=(0.33,5.23,6.98)mm
PLACE B t=(0.33,5.23,4.28)mm
PLACE C t=(0.33,5.23,-0.22)mm
MATE revolute A.f2 <-> C.f0  axis (0,0,1) through (0.33,5.23,9.98)mm
MATE fastened B.f0 <-> C.f0  axis (0,0,-1) through (0.33,5.23,18.28)mm
